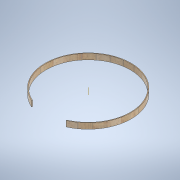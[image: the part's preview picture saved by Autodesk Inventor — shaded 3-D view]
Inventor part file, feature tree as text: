
AUTODESK INVENTOR PART (.ipt)
format: ipt  version: 2020 (Build 240168000, 168)  size: 219,648 bytes
history: native  units: mm
features: extrude x2, sketch x1
ambient origin geometry x8: Origin, YZ Plane, XZ Plane, XY Plane, X Axis, Y Axis, Z Axis, Center Point
bodies: Body1 (feature_tree)
feature tree (3):
  extrude  "Extrusion3"  Depth=10.0mm
  sketch  "Sketch3"  dims[d15=30.0mm d16=0.0mm d40=3.25mm d52=4.363323mm d60=0.872665mm d61=12.566371mm d62=13.439035mm d84=459.42mm d85=467.42mm d87=150.07mm d88=429.0mm d89=4.363323mm d90=1.919862mm d91=1.919862mm d157=10.0mm d158=0.0mm d174=0.5mm d175=0.872665mm d176=0.5mm d177=0.872665mm]
  extrude  "Extrusion10"  Depth=10.0mm
